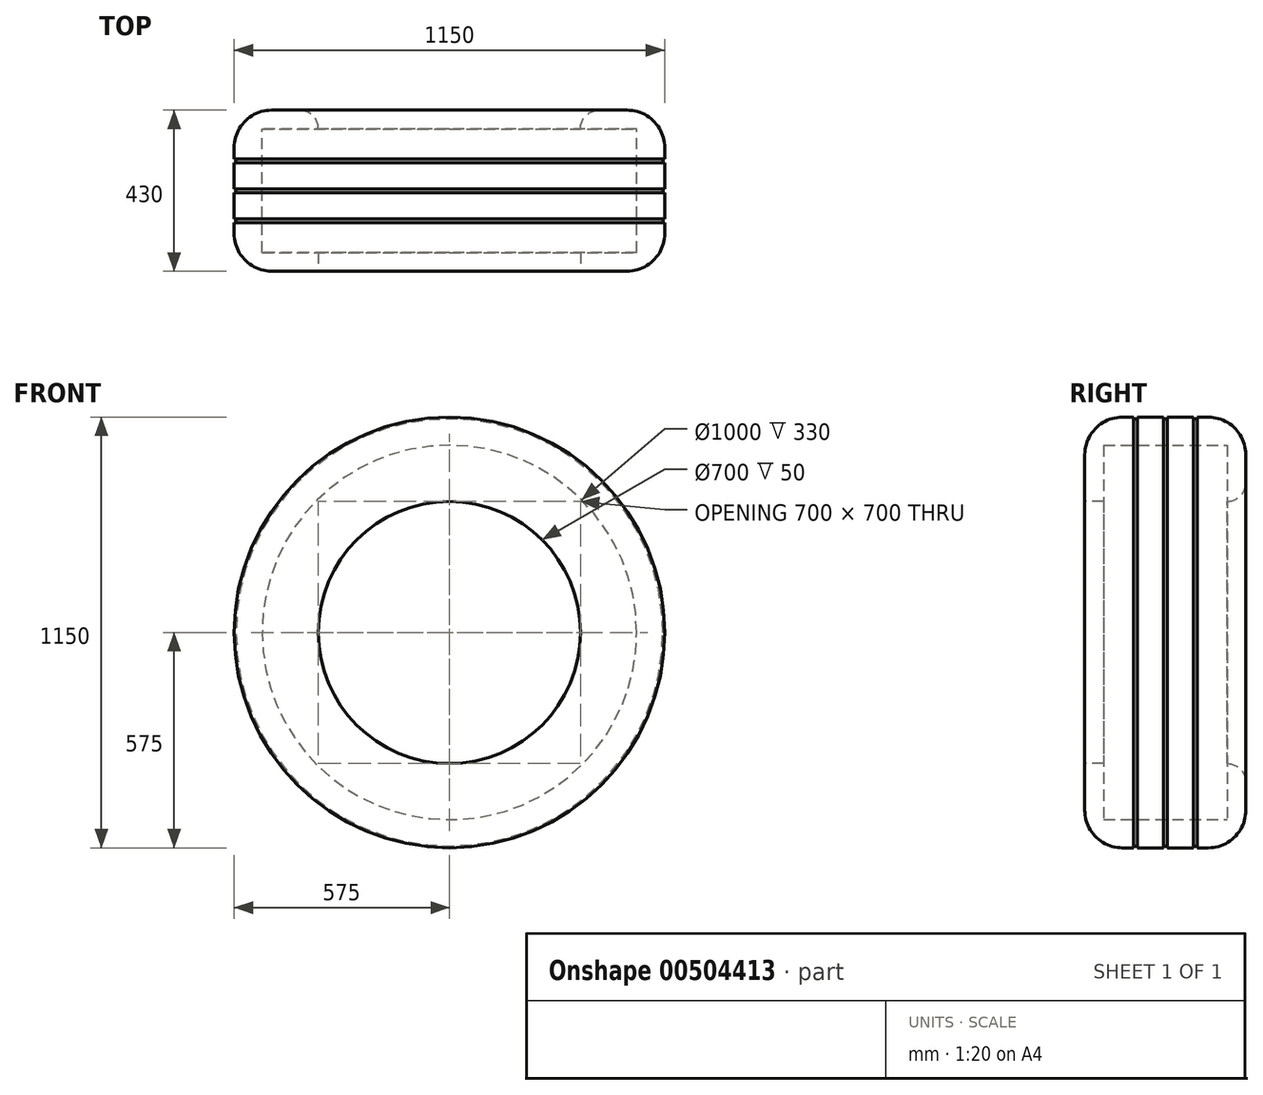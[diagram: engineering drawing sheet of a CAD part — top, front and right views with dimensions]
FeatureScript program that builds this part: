
annotation { "Feature Type Name" : "Feature", "Feature Type Description" : "" }
export const myFeature = defineFeature(function(context is Context, id is Id, definition is map)
    precondition{}
    {
        {
            var Q0;
            Q0=qCreatedBy(makeId("Front.planeOp"),FACE);
            var sketch = newSketch(context, id + "F0", { "sketchPlane" : qUnion([Q0])});
            skCircle(sketch, "E0", {"center": v(0, 0) * mm, "radius": 575 * mm});
            skSolve(sketch);
        }
        {
            var Q0;
            Q0=makeQuery(id+"F0.imprint","IMPRINT",FACE,{"disambiguationData":[TD([[makeQuery(id+"F0.imprint","IMPRINT",EDGE,{"derivedFrom":sQuery(id+"F0.wireOp",EDGE,"E0")}),1.0]])]});
            extrude(context, id + "F1", {"entities" : qUnion([Q0]), "depth" : 430 * mm, "offsetDistance" : 25 * mm});
        }
        {
            var Q0;
            Q0=makeQuery(id+"F1.opExtrude","CAP_FACE",FACE,{"disambiguationData":[OSD([sQuery(id+"F0.wireOp",EDGE,"E0")])],"isStart":false});
            var sketch = newSketch(context, id + "F2", { "sketchPlane" : qUnion([Q0])});
            skCircle(sketch, "E1", {"center": v(0, 0) * mm, "radius": 350 * mm});
            skSolve(sketch);
        }
        {
            var Q0;
            Q0=makeQuery(id+"F2.imprint","IMPRINT",FACE,{"disambiguationData":[TD([[makeQuery(id+"F2.imprint","IMPRINT",EDGE,{"derivedFrom":sQuery(id+"F2.wireOp",EDGE,"E1")}),1.0]])]});
            extrude(context, id + "F3", {"entities" : qUnion([Q0]), "operationType" : NewBodyOperationType.REMOVE, "oppositeDirection" : true, "depth" : 500 * mm, "offsetDistance" : 25 * mm});
        }
        {
            var Q0;
            Q0=makeQuery(id+"F1.opExtrude","CAP_EDGE",EDGE,{"disambiguationData":[OSD([sQuery(id+"F0.wireOp",EDGE,"E0")])],"isStart":false});
            var Q1;
            Q1=makeQuery(id+"F1.opExtrude","CAP_EDGE",EDGE,{"disambiguationData":[OSD([sQuery(id+"F0.wireOp",EDGE,"E0")])],"isStart":true});
            fillet(context, id + "F4", {"entities" : qUnion([Q0, Q1]), "radius" : 100 * mm, "tangentPropagation" : true, "allowEdgeOverflow" : false});
        }
        {
            var Q0;
            Q0=makeQuery(id+"F3.boolean.opBoolean","COPY",EDGE,{"derivedFrom":makeQuery(id+"F3.opExtrude","CAP_EDGE",EDGE,{"disambiguationData":[OSD([sQuery(id+"F2.wireOp",EDGE,"E1")])],"isStart":true})});
            var Q1;
            Q1=makeQuery(id+"F3.boolean.opBoolean","INTERSECT",EDGE,{"derivedFrom":[makeQuery(id+"F1.opExtrude","CAP_FACE",FACE,{"disambiguationData":[OSD([sQuery(id+"F0.wireOp",EDGE,"E0")])],"isStart":true}),makeQuery(id+"F3.opExtrude","SWEPT_FACE",FACE,{"disambiguationData":[OSD([sQuery(id+"F2.wireOp",EDGE,"E1")])]})]});
            fillet(context, id + "F5", {"entities" : qUnion([Q0, Q1]), "radius" : 50 * mm, "tangentPropagation" : true, "allowEdgeOverflow" : false});
        }
        {
            var Q0;
            Q0=qCreatedBy(makeId("Top.planeOp"),FACE);
            var sketch = newSketch(context, id + "F6", { "sketchPlane" : qUnion([Q0])});
            skLineSegment(sketch, "E2", {"start": v(0, 0) * mm, "end": v(350, 0) * mm});
            skLineSegment(sketch, "E3", {"start": v(350, 0) * mm, "end": v(350, -50) * mm});
            skLineSegment(sketch, "E4", {"start": v(350, -50) * mm, "end": v(500, -50) * mm});
            skLineSegment(sketch, "E5", {"start": v(500, -50) * mm, "end": v(500, -380) * mm});
            skLineSegment(sketch, "E6", {"start": v(500, -380) * mm, "end": v(350, -380) * mm});
            skLineSegment(sketch, "E7", {"start": v(350, -380) * mm, "end": v(350, -430) * mm});
            skLineSegment(sketch, "E8", {"start": v(350, -430) * mm, "end": v(0, -430) * mm});
            skLineSegment(sketch, "E9", {"start": v(0, -430) * mm, "end": v(0, 0) * mm});
            skLineSegment(sketch, "E10.bottom", {"start": v(684.68, -130) * mm, "end": v(570, -130) * mm});
            skLineSegment(sketch, "E10.top", {"start": v(684.68, -140) * mm, "end": v(570, -140) * mm});
            skLineSegment(sketch, "E10.left", {"start": v(684.68, -130) * mm, "end": v(684.68, -140) * mm});
            skLineSegment(sketch, "E10.right", {"start": v(570, -130) * mm, "end": v(570, -140) * mm});
            skLineSegment(sketch, "E11.bottom", {"start": v(727.07, -210) * mm, "end": v(570, -210) * mm});
            skLineSegment(sketch, "E11.top", {"start": v(727.07, -220) * mm, "end": v(570, -220) * mm});
            skLineSegment(sketch, "E11.left", {"start": v(727.07, -210) * mm, "end": v(727.07, -220) * mm});
            skLineSegment(sketch, "E11.right", {"start": v(570, -210) * mm, "end": v(570, -220) * mm});
            skLineSegment(sketch, "E12.bottom", {"start": v(718.08, -290) * mm, "end": v(570, -290) * mm});
            skLineSegment(sketch, "E12.top", {"start": v(718.08, -300) * mm, "end": v(570, -300) * mm});
            skLineSegment(sketch, "E12.left", {"start": v(718.08, -290) * mm, "end": v(718.08, -300) * mm});
            skLineSegment(sketch, "E12.right", {"start": v(570, -290) * mm, "end": v(570, -300) * mm});
            skSolve(sketch);
        }
        {
            var Q0;
            Q0=makeQuery(id+"F6.imprint","IMPRINT",FACE,{"disambiguationData":[TD([[makeQuery(id+"F6.imprint","IMPRINT",EDGE,{"derivedFrom":sQuery(id+"F6.wireOp",EDGE,"E2")}),-1.0]])]});
            var Q1;
            Q1=makeQuery(id+"F6.imprint","IMPRINT",FACE,{"disambiguationData":[TD([[makeQuery(id+"F6.imprint","IMPRINT",EDGE,{"derivedFrom":sQuery(id+"F6.wireOp",EDGE,"E12.bottom")}),1.0]])]});
            var Q2;
            Q2=makeQuery(id+"F6.imprint","IMPRINT",FACE,{"disambiguationData":[TD([[makeQuery(id+"F6.imprint","IMPRINT",EDGE,{"derivedFrom":sQuery(id+"F6.wireOp",EDGE,"E11.bottom")}),1.0]])]});
            var Q3;
            Q3=makeQuery(id+"F6.imprint","IMPRINT",FACE,{"disambiguationData":[TD([[makeQuery(id+"F6.imprint","IMPRINT",EDGE,{"derivedFrom":sQuery(id+"F6.wireOp",EDGE,"E10.bottom")}),1.0]])]});
            var Q4;
            Q4=sQuery(id+"F6.wireOp",EDGE,"E9");
            revolve(context, id + "F7", {"operationType" : NewBodyOperationType.REMOVE, "entities" : qUnion([Q0, Q1, Q2, Q3]), "axis" : qUnion([Q4]), "revolveType" : RevolveType.FULL, "oppositeDirection" : true});
        }
    });
